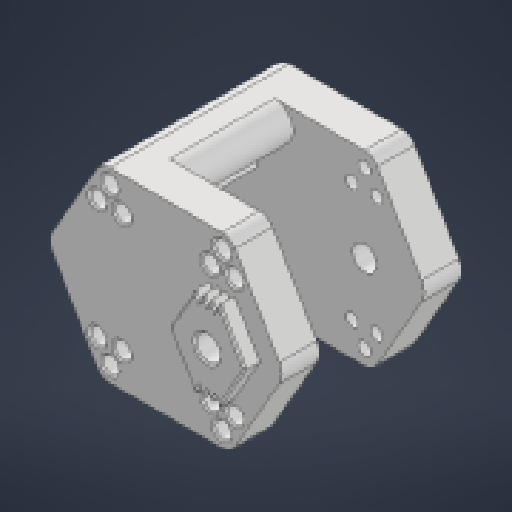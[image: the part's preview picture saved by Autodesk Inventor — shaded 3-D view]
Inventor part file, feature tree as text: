
AUTODESK INVENTOR PART (.ipt)
format: ipt  version: 2024.1 (Build 281209000, 209)  size: 435,200 bytes
history: native  units: in
note: dims shown in document units (in); Inventor stores cm internally (conversion verified against a paired STEP export)
features: extrude x6, other x3, chamfer x2, sketch x1, mirror x1, fillet x1, reference x1
ambient origin geometry x8: Origin, YZ Plane, XZ Plane, XY Plane, X Axis, Y Axis, Z Axis, Center Point
bodies: Solid1 (feature_tree)
feature tree (15):
  sketch  "Sketch1"  dims[d0=0.219in d1=0.219in d2=0.1654in d3=0.1654in d4=0.2in d5=0.2in d6=0.219in d7=0.1654in d8=0.25in d9=0.4in d10=0.3268in d11=0.5906in d12=0.5in d13=0.0in d14=0.2in d15=0.0in d16=0.2488in d17=0.5in d18=0.0in d19=0.0in d20=4.0in d21=0.0in d22=0.2756in d23=0.0in d24=0.025in d25=0.125in d26=45.0deg d27=2.5in d29=0.75in d30=1.0in d31=45.0deg d32=0.7874in d34=1.5in d35=0.3937in d37=1.0in d39=0.4in d40=0.4in d42=0.05in d43=1.1998in d44=0.0in d45=0.25in d46=0.025in d47=0.125in d48=45.0deg]
  extrude  "Extrusion1"  Depth=0.25in
  extrude  "Extrusion2"  Depth=0.25in
  extrude  "Extrusion3"  Depth=0.25in
  extrude  "Extrusion6"  Depth=0.2in
  extrude  "Extrusion4"  Depth=0.2in
  extrude  "Extrusion5"  Depth=0.25in
  chamfer  "Chamfer1"  Distance=0.1654in
  mirror  "Mirror1"
  fillet  "Fillet1"  Radius=0.25in
  chamfer  "Chamfer2"  Distance=0.4in
  reference  "Reference1"
  other  "<userpath>\Documents\School\FallCAD\Trebuchet\Trebuchet.iam"
  other  "Trebuchet.iam"
  other  "WeightArm:1"
